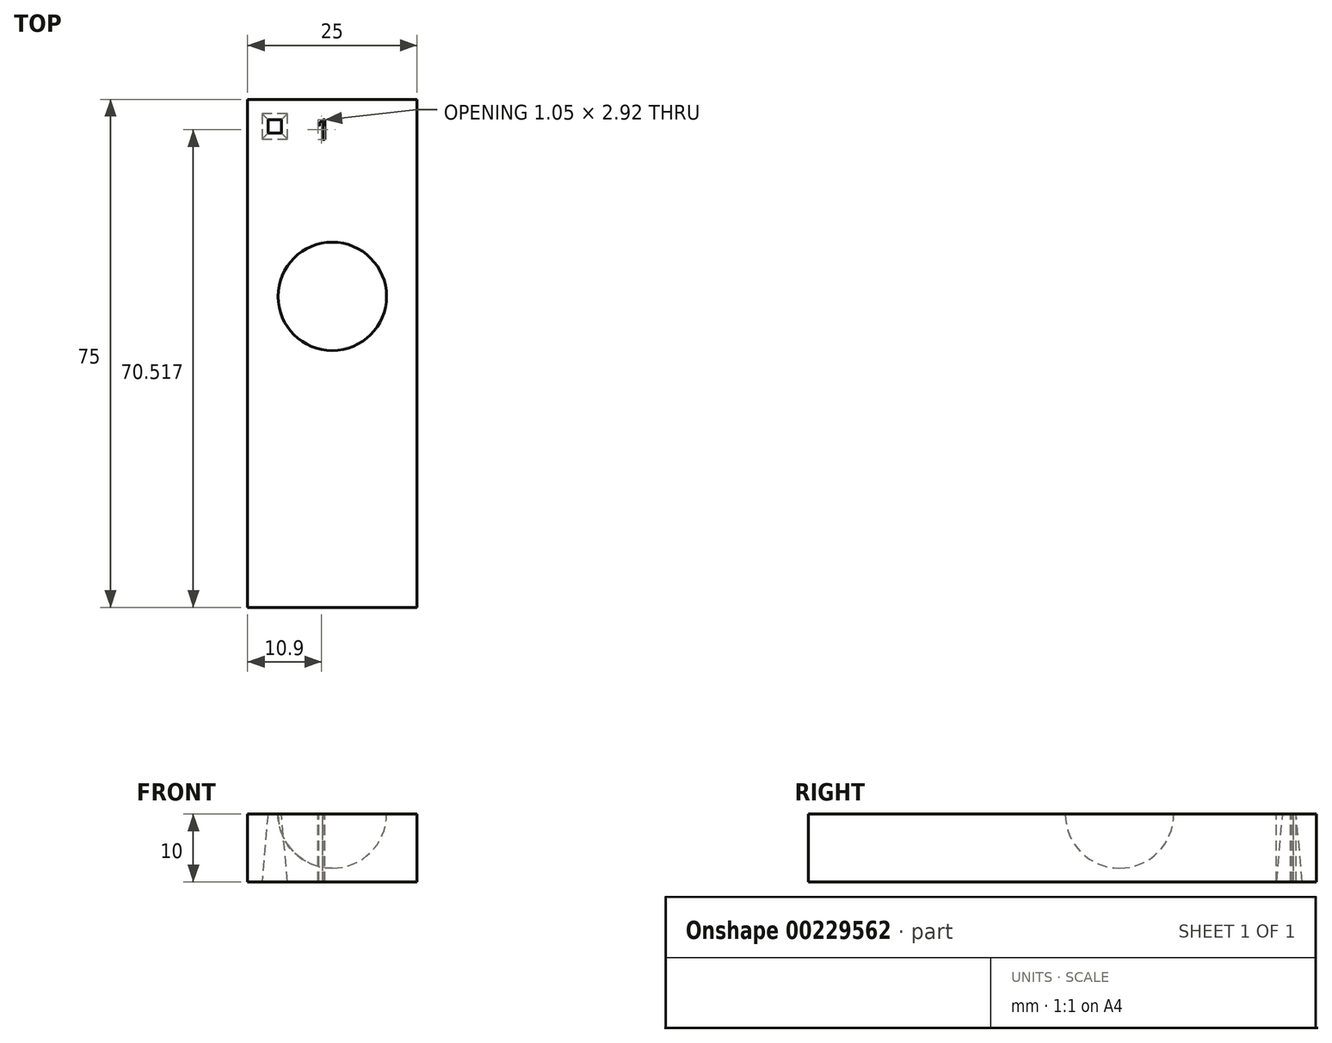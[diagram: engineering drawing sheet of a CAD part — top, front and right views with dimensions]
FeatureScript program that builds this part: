
annotation { "Feature Type Name" : "Feature", "Feature Type Description" : "" }
export const myFeature = defineFeature(function(context is Context, id is Id, definition is map)
    precondition{}
    {
        {
            var Q0;
            Q0=qCreatedBy(makeId("Top.planeOp"),FACE);
            var sketch = newSketch(context, id + "F0", { "sketchPlane" : qUnion([Q0])});
            skLineSegment(sketch, "E0.bottom", {"start": v(22.33, 29.08) * mm, "end": v(47.33, 29.08) * mm});
            skLineSegment(sketch, "E0.top", {"start": v(22.33, -45.92) * mm, "end": v(47.33, -45.92) * mm});
            skLineSegment(sketch, "E0.left", {"start": v(22.33, 29.08) * mm, "end": v(22.33, -45.92) * mm});
            skLineSegment(sketch, "E0.right", {"start": v(47.33, 29.08) * mm, "end": v(47.33, -45.92) * mm});
            skSolve(sketch);
        }
        {
            var Q0;
            Q0 = qSketchRegion(id + "F0", true);
            extrude(context, id + "F1", {"entities" : qUnion([Q0]), "oppositeDirection" : true, "depth" : 10 * mm});
        }
        {
            var Q0;
            Q0=qCreatedBy(makeId("Top.planeOp"),FACE);
            var sketch = newSketch(context, id + "F2", { "sketchPlane" : qUnion([Q0])});
            skLineSegment(sketch, "E1.bottom", {"start": v(25.33, 26.08) * mm, "end": v(27.33, 26.08) * mm});
            skLineSegment(sketch, "E1.top", {"start": v(25.33, 24.08) * mm, "end": v(27.33, 24.08) * mm});
            skLineSegment(sketch, "E1.left", {"start": v(25.33, 26.08) * mm, "end": v(25.33, 24.08) * mm});
            skLineSegment(sketch, "E1.right", {"start": v(27.33, 26.08) * mm, "end": v(27.33, 24.08) * mm});
            skSolve(sketch);
        }
        {
            var Q0;
            Q0 = qSketchRegion(id + "F2", true);
            extrude(context, id + "F3", {"entities" : qUnion([Q0]), "operationType" : NewBodyOperationType.REMOVE, "oppositeDirection" : true, "depth" : 20 * mm, "hasDraft" : true, "draftAngle" : 5 * degree});
        }
        {
            var Q0;
            Q0=qCreatedBy(makeId("Top.planeOp"),FACE);
            var sketch = newSketch(context, id + "F4", { "sketchPlane" : qUnion([Q0])});
            skText(sketch, "E2", { "text": "1", "fontName": "OpenSans-Regular.ttf"});
            const initialGuessF4  = {"E2": [0.03233, 0.02314, 1, 0, 0.00294]};
            skSetInitialGuess(sketch, initialGuessF4);
            skSolve(sketch);
        }
        {
            var Q0;
            Q0 = qSketchRegion(id + "F4", true);
            extrude(context, id + "F5", {"entities" : qUnion([Q0]), "operationType" : NewBodyOperationType.REMOVE, "oppositeDirection" : true, "depth" : 20 * mm});
        }
        {
            var Q0;
            Q0=qCreatedBy(makeId("Front.planeOp"),FACE);
            var sketch = newSketch(context, id + "F6", { "sketchPlane" : qUnion([Q0])});
            skArc(sketch, "E3", {"start": v(26.83, 0) * mm, "mid": v(29.17, -5.66) * mm, "end": v(34.83, -8) * mm});
            skLineSegment(sketch, "E4", {"start": v(34.83, 0) * mm, "end": v(34.83, -9.8) * mm, "construction": true});
            skLineSegment(sketch, "E5", {"start": v(26.83, 0) * mm, "end": v(34.83, 0) * mm});
            skLineSegment(sketch, "E6", {"start": v(34.83, 0) * mm, "end": v(34.83, -8) * mm});
            skSolve(sketch);
        }
        {
            var Q0;
            Q0 = qSketchRegion(id + "F6", true);
            var Q1;
            Q1=sQuery(id+"F6.wireOp",EDGE,"E4");
            revolve(context, id + "F7", {"operationType" : NewBodyOperationType.REMOVE, "entities" : qUnion([Q0]), "axis" : qUnion([Q1]), "revolveType" : RevolveType.FULL});
        }
    });
